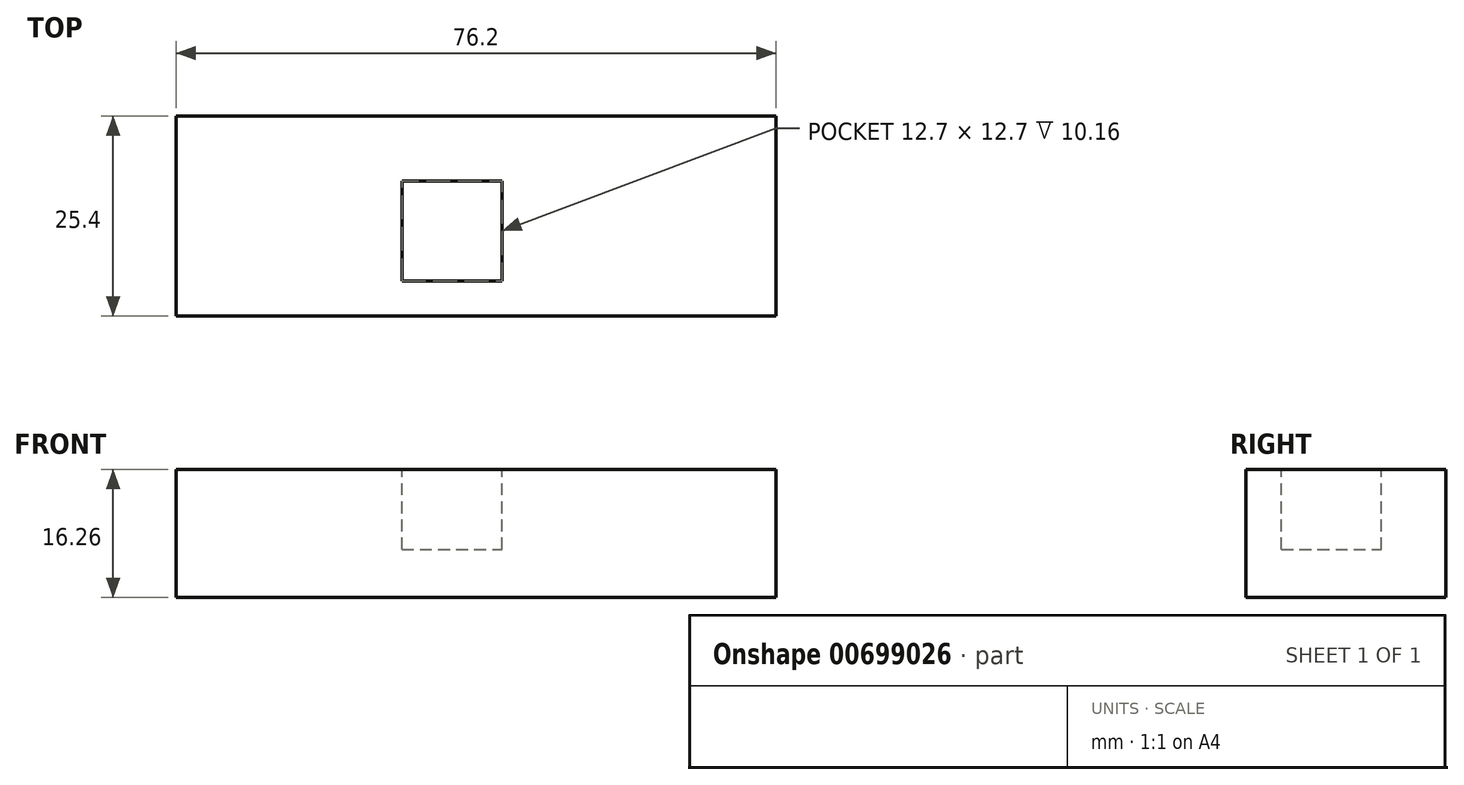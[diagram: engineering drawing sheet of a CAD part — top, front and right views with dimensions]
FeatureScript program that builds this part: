
annotation { "Feature Type Name" : "Feature", "Feature Type Description" : "" }
export const myFeature = defineFeature(function(context is Context, id is Id, definition is map)
    precondition{}
    {
        {
            var Q0;
            Q0=qCreatedBy(makeId("Top.planeOp"),FACE);
            var sketch = newSketch(context, id + "F0", { "sketchPlane" : qUnion([Q0])});
            skLineSegment(sketch, "E0.bottom", {"start": v(0, 0) * mm, "end": v(-76.2, 0) * mm});
            skLineSegment(sketch, "E0.top", {"start": v(0, 25.4) * mm, "end": v(-76.2, 25.4) * mm});
            skLineSegment(sketch, "E0.left", {"start": v(0, 0) * mm, "end": v(0, 25.4) * mm});
            skLineSegment(sketch, "E0.right", {"start": v(-76.2, 0) * mm, "end": v(-76.2, 25.4) * mm});
            skSolve(sketch);
        }
        {
            var Q0;
            Q0=makeQuery(id+"F0.imprint","IMPRINT",FACE,{"disambiguationData":[TD([[makeQuery(id+"F0.imprint","IMPRINT",EDGE,{"derivedFrom":sQuery(id+"F0.wireOp",EDGE,"E0.bottom")}),-1.0]])]});
            extrude(context, id + "F1", {"entities" : qUnion([Q0]), "depth" : 1.02 * mm, "offsetDistance" : 25.4 * mm});
        }
        {
            var Q0;
            Q0=makeQuery(id+"F1.opExtrude","CAP_FACE",FACE,{"disambiguationData":[OSD([sQuery(id+"F0.wireOp",EDGE,"E0.bottom"),sQuery(id+"F0.wireOp",EDGE,"E0.top"),sQuery(id+"F0.wireOp",EDGE,"E0.left"),sQuery(id+"F0.wireOp",EDGE,"E0.right")])],"isStart":false});
            extrude(context, id + "F2", {"entities" : qUnion([Q0]), "operationType" : NewBodyOperationType.ADD, "depth" : 15.24 * mm, "offsetDistance" : 25.4 * mm});
        }
        {
            var Q0;
            Q0=makeQuery(id+"F2.opExtrude","CAP_FACE",FACE,{"disambiguationData":[OSD([sQuery(id+"F0.wireOp",EDGE,"E0.bottom"),sQuery(id+"F0.wireOp",EDGE,"E0.top"),sQuery(id+"F0.wireOp",EDGE,"E0.left"),sQuery(id+"F0.wireOp",EDGE,"E0.right")])],"isStart":false});
            var sketch = newSketch(context, id + "F3", { "sketchPlane" : qUnion([Q0])});
            skLineSegment(sketch, "E1.bottom", {"start": v(-47.53, 4.47) * mm, "end": v(-34.83, 4.47) * mm});
            skLineSegment(sketch, "E1.top", {"start": v(-47.53, 17.17) * mm, "end": v(-34.83, 17.17) * mm});
            skLineSegment(sketch, "E1.left", {"start": v(-47.53, 4.47) * mm, "end": v(-47.53, 17.17) * mm});
            skLineSegment(sketch, "E1.right", {"start": v(-34.83, 4.47) * mm, "end": v(-34.83, 17.17) * mm});
            skSolve(sketch);
        }
        {
            var Q0;
            Q0=makeQuery(id+"F3.imprint","IMPRINT",FACE,{"disambiguationData":[TD([[makeQuery(id+"F3.imprint","IMPRINT",EDGE,{"derivedFrom":sQuery(id+"F3.wireOp",EDGE,"E1.bottom")}),1.0]])]});
            extrude(context, id + "F4", {"entities" : qUnion([Q0]), "operationType" : NewBodyOperationType.REMOVE, "oppositeDirection" : true, "depth" : 10.16 * mm, "offsetDistance" : 25.4 * mm});
        }
    });
